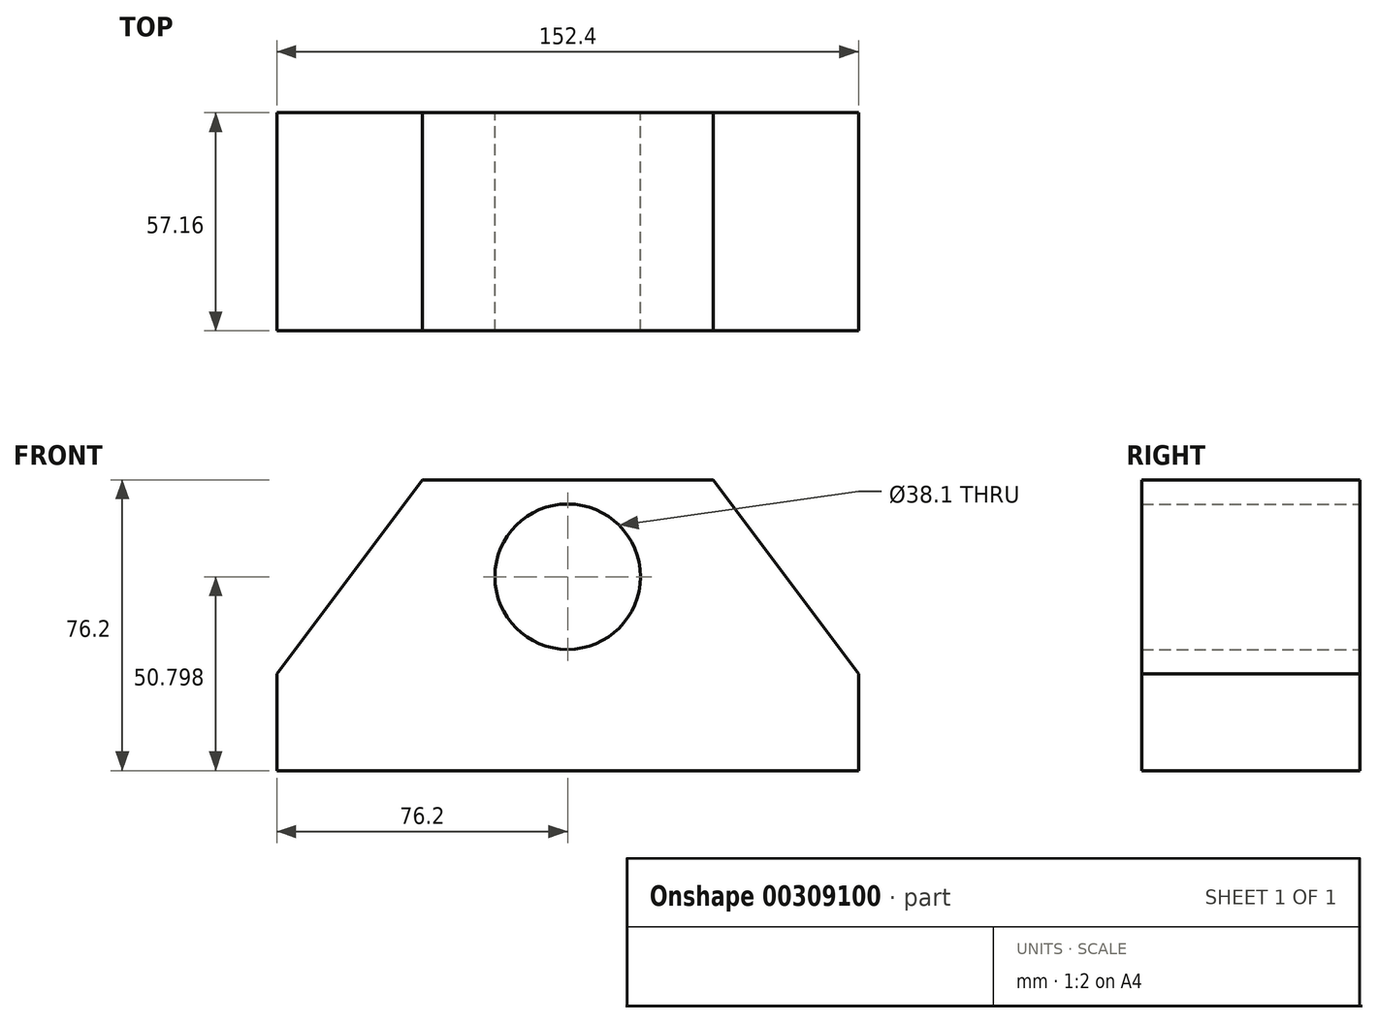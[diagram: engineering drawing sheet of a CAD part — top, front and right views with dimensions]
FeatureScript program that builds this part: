
annotation { "Feature Type Name" : "Feature", "Feature Type Description" : "" }
export const myFeature = defineFeature(function(context is Context, id is Id, definition is map)
    precondition{}
    {
        {
            var Q0;
            Q0=qCreatedBy(makeId("Front.planeOp"),FACE);
            var sketch = newSketch(context, id + "F0", { "sketchPlane" : qUnion([Q0])});
            skLineSegment(sketch, "E0", {"start": v(-76.2, -10.07) * mm, "end": v(-76.2, -35.47) * mm});
            skLineSegment(sketch, "E1", {"start": v(-76.2, -35.47) * mm, "end": v(76.2, -35.47) * mm});
            skLineSegment(sketch, "E2", {"start": v(76.2, -35.47) * mm, "end": v(76.2, -10.07) * mm});
            skLineSegment(sketch, "E3", {"start": v(76.2, -10.07) * mm, "end": v(38.1, 40.73) * mm});
            skLineSegment(sketch, "E4", {"start": v(-76.2, -10.07) * mm, "end": v(-38.1, 40.73) * mm});
            skLineSegment(sketch, "E5", {"start": v(-38.1, 40.73) * mm, "end": v(38.1, 40.73) * mm});
            skCircle(sketch, "E6", {"center": v(0, 15.33) * mm, "radius": 19.05 * mm});
            skSolve(sketch);
        }
        {
            var Q0;
            Q0=makeQuery(id+"F0.imprint","IMPRINT",FACE,{"disambiguationData":[TD([[makeQuery(id+"F0.imprint","IMPRINT",EDGE,{"derivedFrom":sQuery(id+"F0.wireOp",EDGE,"E0")}),1.0]])]});
            extrude(context, id + "F1", {"entities" : qUnion([Q0]), "depth" : 57.15 * mm, "symmetric" : true});
        }
    });
